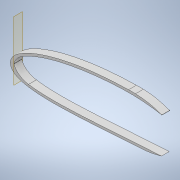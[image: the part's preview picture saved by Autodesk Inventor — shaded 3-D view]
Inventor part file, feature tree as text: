
AUTODESK INVENTOR PART (.ipt)
format: ipt  version: 2022.1 (Build 261234020, 234B)  size: 541,696 bytes
history: native  units: mm
features: sketch x6, extrude x5, thicken_offset x4, projected_geometry x3, shell x1, plane x1, other x1, fillet x1
ambient origin geometry x8: Origin, YZ Plane, XZ Plane, XY Plane, X Axis, Y Axis, Z Axis, Center Point
bodies: Solid1 (feature_tree)
feature tree (22):
  extrude  "Extrusion1"  Depth=3.0mm
  shell  "Shell1"  Thickness=1.0mm
  thicken_offset  "Thicken1"
  extrude  "Extrusion27"  TaperAngle=0.0deg  [1 undecoded]
  thicken_offset  "Thicken3"
  extrude  "Extrusion29"  Depth=20.0mm
  plane  "Work Plane5"
  other  "Bend Part2"
  thicken_offset  "Thicken5"
  extrude  "Extrusion30"  Depth=10.0mm TaperAngle=0.0deg
  thicken_offset  "Thicken6"
  extrude  "Extrusion31"  Depth=1.0mm
  fillet  "Fillet6"  Radius=1.0mm
  sketch  "Sketch3"  dims[d0=10.0mm d1=0.0mm d2=3.0mm d159=1.0mm d160=2.0mm]
  sketch  "Sketch48"  dims[d236=190.0mm d237=0.0mm d238=0.0mm]
  sketch  "Sketch55"  dims[d249=2.0mm d250=1.0mm d254=20.0mm]
  projected_geometry  "Projected Loop32"
  sketch  "Sketch57"  dims[d255=8.0mm d256=10.0mm d257=0.0mm]
  sketch  "Sketch58"  dims[d262=10.0mm d263=0.349066mm d264=1.0mm d265=1.0mm]
  projected_geometry  "Projected Loop34"
  sketch  "Sketch59"  dims[d268=50.0mm d269=3.0mm d270=10.0mm d271=0.0mm d272=2.0mm d273=2.0mm d274=3.0mm d275=200.0mm d276=10.0mm d277=0.0mm d278=100.0mm]
  projected_geometry  "Projected Loop35"
note: 1 required parameter value undecoded (feature->parameter linkage not recoverable at this tier; creation-order binding heuristic only, values carry confidence <= 0.55)
